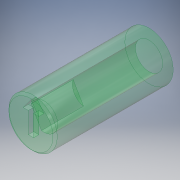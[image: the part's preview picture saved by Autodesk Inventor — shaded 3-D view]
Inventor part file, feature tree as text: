
AUTODESK INVENTOR PART (.ipt)
format: ipt  version: 2017 SP1 (Build 210196100, 196)  size: 146,944 bytes
history: native  units: in
note: dims shown in document units (in); Inventor stores cm internally (conversion verified against a paired STEP export)
features: extrude x4, sketch x4, chamfer x1, projected_geometry x1
ambient origin geometry x8: Origin, YZ Plane, XZ Plane, XY Plane, X Axis, Y Axis, Z Axis, Center Point
bodies: Solid1 (feature_tree)
feature tree (10):
  extrude  "Extrusion1"  Depth=0.0125in
  extrude  "Extrusion2"  Depth=1.0in
  extrude  "Extrusion3"  Depth=0.2in
  chamfer  "Chamfer1"  Distance=0.05in
  extrude  "Extrusion6"  Depth=0.4in
  sketch  "Sketch1"  dims[d0=0.235in d2=0.0125in]
  sketch  "Sketch2"  dims[d3=1.0in d4=0.0in d5=0.1in]
  sketch  "Sketch3"  dims[d6=0.125in d7=0.0in d8=0.2in]
  sketch  "Sketch6"  dims[d9=0.1in d10=0.05in d11=0.15in d12=0.05in d13=0.0in d20=0.02in d21=0.125in d22=45.0deg d24=60.0deg d26=0.215in d27=0.4in d28=0.0in]
  projected_geometry  "Projected Loop4"
